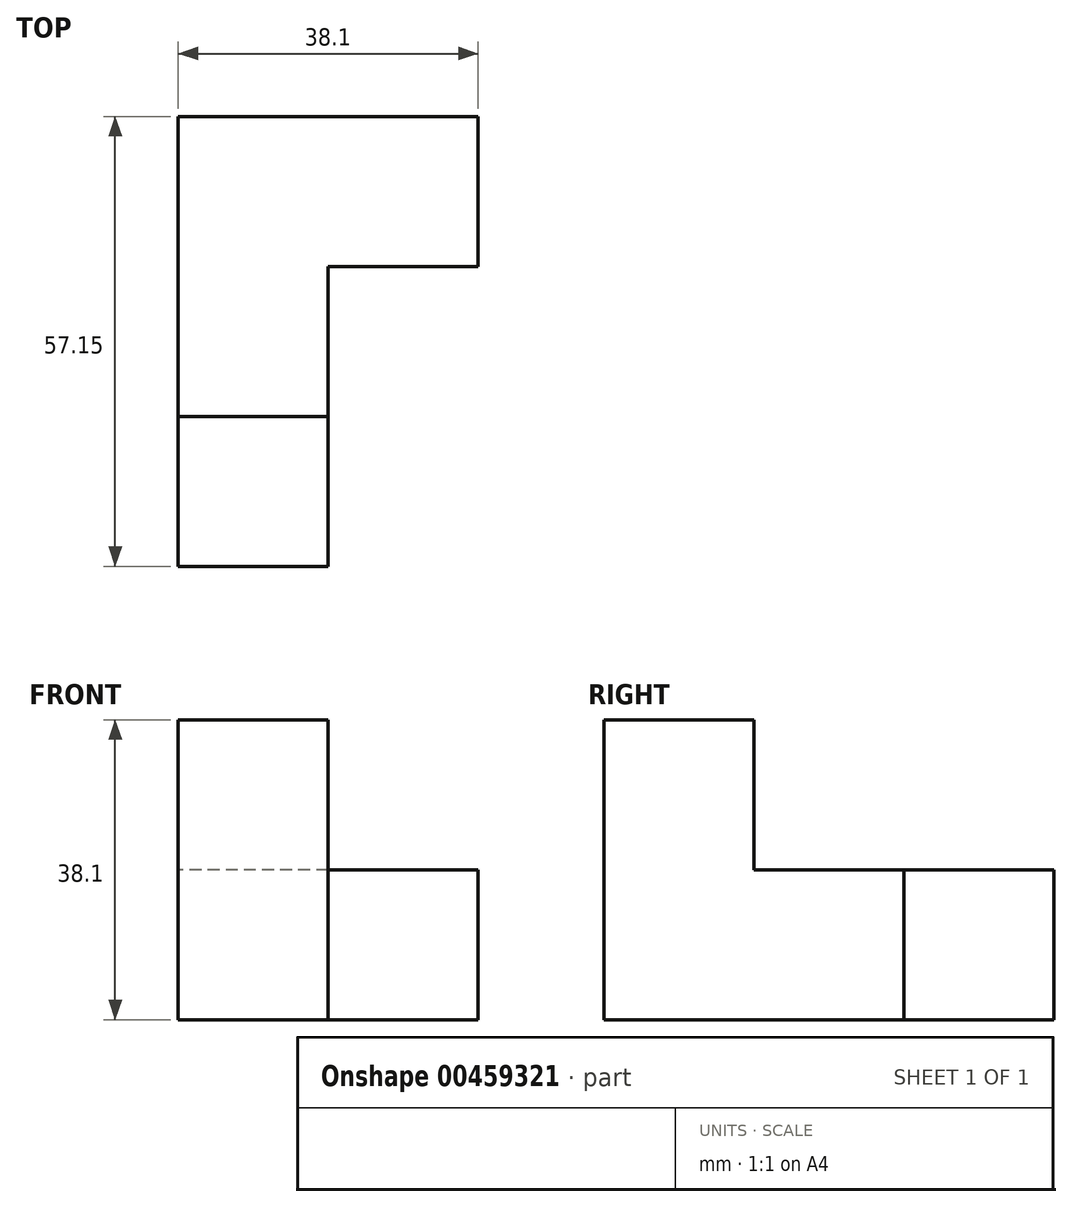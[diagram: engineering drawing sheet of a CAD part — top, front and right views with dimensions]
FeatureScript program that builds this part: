
annotation { "Feature Type Name" : "Feature", "Feature Type Description" : "" }
export const myFeature = defineFeature(function(context is Context, id is Id, definition is map)
    precondition{}
    {
        {
            var Q0;
            Q0=qCreatedBy(makeId("Top.planeOp"),FACE);
            var sketch = newSketch(context, id + "F0", { "sketchPlane" : qUnion([Q0])});
            skLineSegment(sketch, "E0", {"start": v(0, 0) * mm, "end": v(0, 19.05) * mm});
            skLineSegment(sketch, "E1", {"start": v(0, 19.05) * mm, "end": v(-38.1, 19.05) * mm});
            skLineSegment(sketch, "E2", {"start": v(-38.1, 19.05) * mm, "end": v(-38.1, -38.1) * mm});
            skLineSegment(sketch, "E3", {"start": v(-38.1, -38.1) * mm, "end": v(-19.05, -38.1) * mm});
            skLineSegment(sketch, "E4", {"start": v(-19.05, -38.1) * mm, "end": v(-19.05, 0) * mm});
            skLineSegment(sketch, "E5", {"start": v(-19.05, 0) * mm, "end": v(0, 0) * mm});
            skLineSegment(sketch, "E6", {"start": v(-19.05, -19.05) * mm, "end": v(-38.1, -19.05) * mm});
            skSolve(sketch);
        }
        {
            var Q0;
            Q0=makeQuery(id+"F0.imprint","IMPRINT",FACE,{"disambiguationData":[TD([[makeQuery(id+"F0.imprint","IMPRINT",EDGE,{"derivedFrom":sQuery(id+"F0.wireOp",EDGE,"E0")}),1.0]])]});
            extrude(context, id + "F1", {"entities" : qUnion([Q0]), "depth" : 19.05 * mm});
        }
        {
            var Q0;
            {var subQ0=sQuery(id+"F0.wireOp",EDGE,"E3");Q0=makeQuery(id+"F0.imprint","IMPRINT",FACE,{"disambiguationData":[TD([[makeQuery(id+"F0.imprint","IMPRINT",EDGE,{"derivedFrom":subQ0}),1.0]])]});}
            extrude(context, id + "F2", {"entities" : qUnion([Q0]), "operationType" : NewBodyOperationType.ADD, "depth" : 38.1 * mm});
        }
    });
